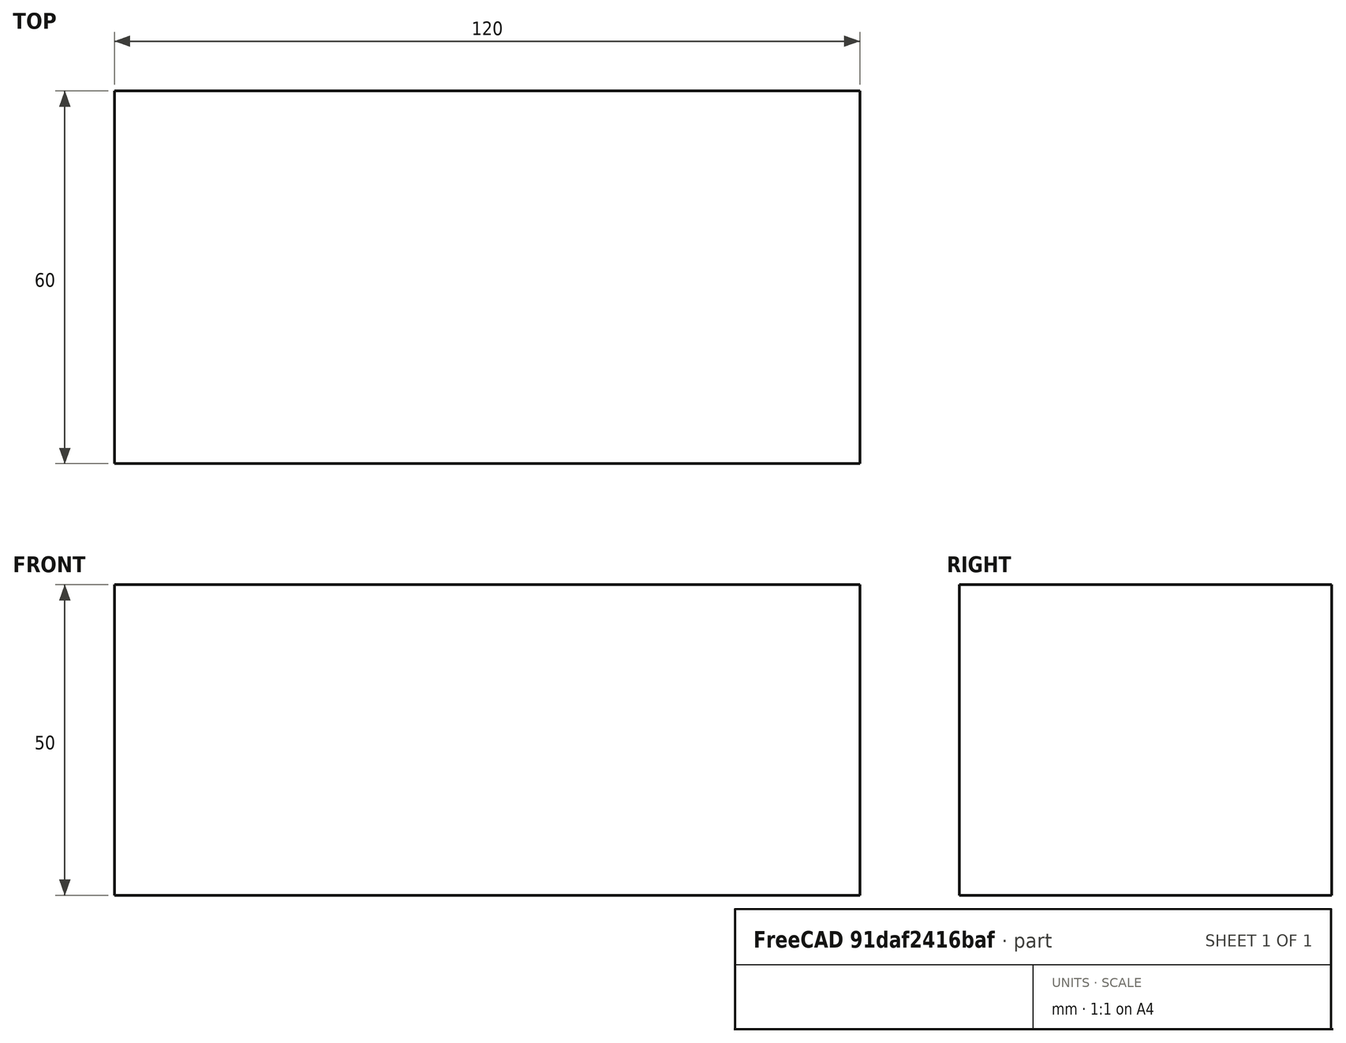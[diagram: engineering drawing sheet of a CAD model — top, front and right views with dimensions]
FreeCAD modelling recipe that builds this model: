
FCSTD DOCUMENT  (FreeCAD 0.15R4671 (Git))
Label: Flat Bar 120x60 EN10058 S235JR
License: All rights reserved
LicenseURL: http://en.wikipedia.org/wiki/All_rights_reserved
objects: Sketcher::SketchObject×1, Part::Extrusion×1
note: 2 computed .brp shape members not serialized (recipe doc carries the construction recipe); baked Part::Feature solids carry a one-line shape summary decoded from their .brp

FEATURE [Sketcher::SketchObject] Sketch
  sketch-geometry (4):
    g0: LineSegment StartX=-60 StartY=-30 StartZ=0 EndX=60 EndY=-30 EndZ=0
    g1: LineSegment StartX=60 StartY=-30 StartZ=0 EndX=60 EndY=30 EndZ=0
    g2: LineSegment StartX=60 StartY=30 StartZ=0 EndX=-60 EndY=30 EndZ=0
    g3: LineSegment StartX=-60 StartY=30 StartZ=0 EndX=-60 EndY=-30 EndZ=0
  constraints (12):
    c: Coincident(g0,g1)
    c: Coincident(g1,g2)
    c: Coincident(g2,g3)
    c: Coincident(g3,g0)
    c: Horizontal(g0)
    c: Horizontal(g2)
    c: Vertical(g1)
    c: Vertical(g3)
    c: Symmetric(g1,g2,g-2)
    c: Symmetric(g0,g1,g-1)
    c: DistanceY(g1) = 60
    c: DistanceX(g0) = 120
FEATURE [Part::Extrusion] Extrude  label="Flat Bar 120x60 EN10058 S235JR"
  Base = -> Sketch
  Dir = (0,0,50)
  Solid = true
